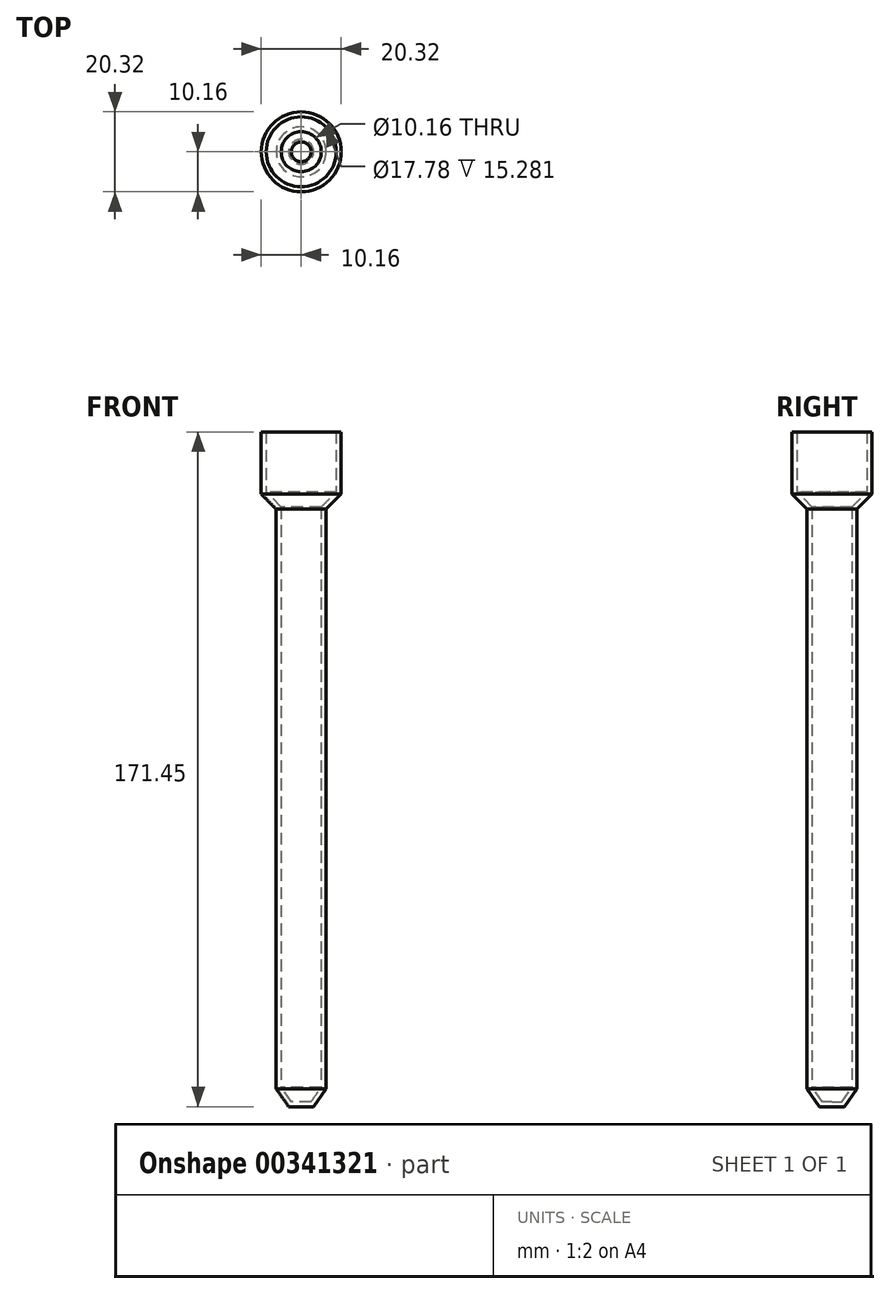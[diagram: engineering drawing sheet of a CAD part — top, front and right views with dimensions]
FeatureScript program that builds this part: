
annotation { "Feature Type Name" : "Feature", "Feature Type Description" : "" }
export const myFeature = defineFeature(function(context is Context, id is Id, definition is map)
    precondition{}
    {
        {
            var Q0;
            Q0=qCreatedBy(makeId("Front.planeOp"),FACE);
            var sketch = newSketch(context, id + "F0", { "sketchPlane" : qUnion([Q0])});
            skLineSegment(sketch, "E0.bottom", {"start": v(0, -41.37) * mm, "end": v(-3.18, -41.37) * mm});
            skLineSegment(sketch, "E0.left", {"start": v(0, -41.37) * mm, "end": v(0, 111.03) * mm});
            skLineSegment(sketch, "E0.right", {"start": v(-6.35, -36.83) * mm, "end": v(-6.35, 110.47) * mm});
            skLineSegment(sketch, "E1", {"start": v(-6.35, -36.83) * mm, "end": v(-3.18, -41.37) * mm});
            skLineSegment(sketch, "E2", {"start": v(-6.35, 110.47) * mm, "end": v(-10.16, 114.28) * mm});
            skLineSegment(sketch, "E3", {"start": v(-10.16, 114.28) * mm, "end": v(-10.16, 130.08) * mm});
            skLineSegment(sketch, "E4", {"start": v(-10.16, 130.08) * mm, "end": v(0, 130.08) * mm});
            skLineSegment(sketch, "E5", {"start": v(0, 130.08) * mm, "end": v(0, 111.03) * mm});
            skSolve(sketch);
        }
        {
            var Q0;
            Q0=makeQuery(id+"F0.imprint","IMPRINT",FACE,{"disambiguationData":[TD([[makeQuery(id+"F0.imprint","IMPRINT",EDGE,{"derivedFrom":sQuery(id+"F0.wireOp",EDGE,"E0.bottom")}),-1.0]])]});
            var Q1;
            Q1=sQuery(id+"F0.wireOp",EDGE,"E0.left");
            revolve(context, id + "F1", {"entities" : qUnion([Q0]), "axis" : qUnion([Q1]), "revolveType" : RevolveType.FULL});
        }
        {
            var Q0;
            Q0=makeQuery(id+"F1.opRevolve","SWEPT_FACE",FACE,{"disambiguationData":[OSD([sQuery(id+"F0.wireOp",EDGE,"E4")])]});
            shell(context, id + "F2", {"entities" : qUnion([Q0]), "thickness" : 1.27 * mm});
        }
    });
